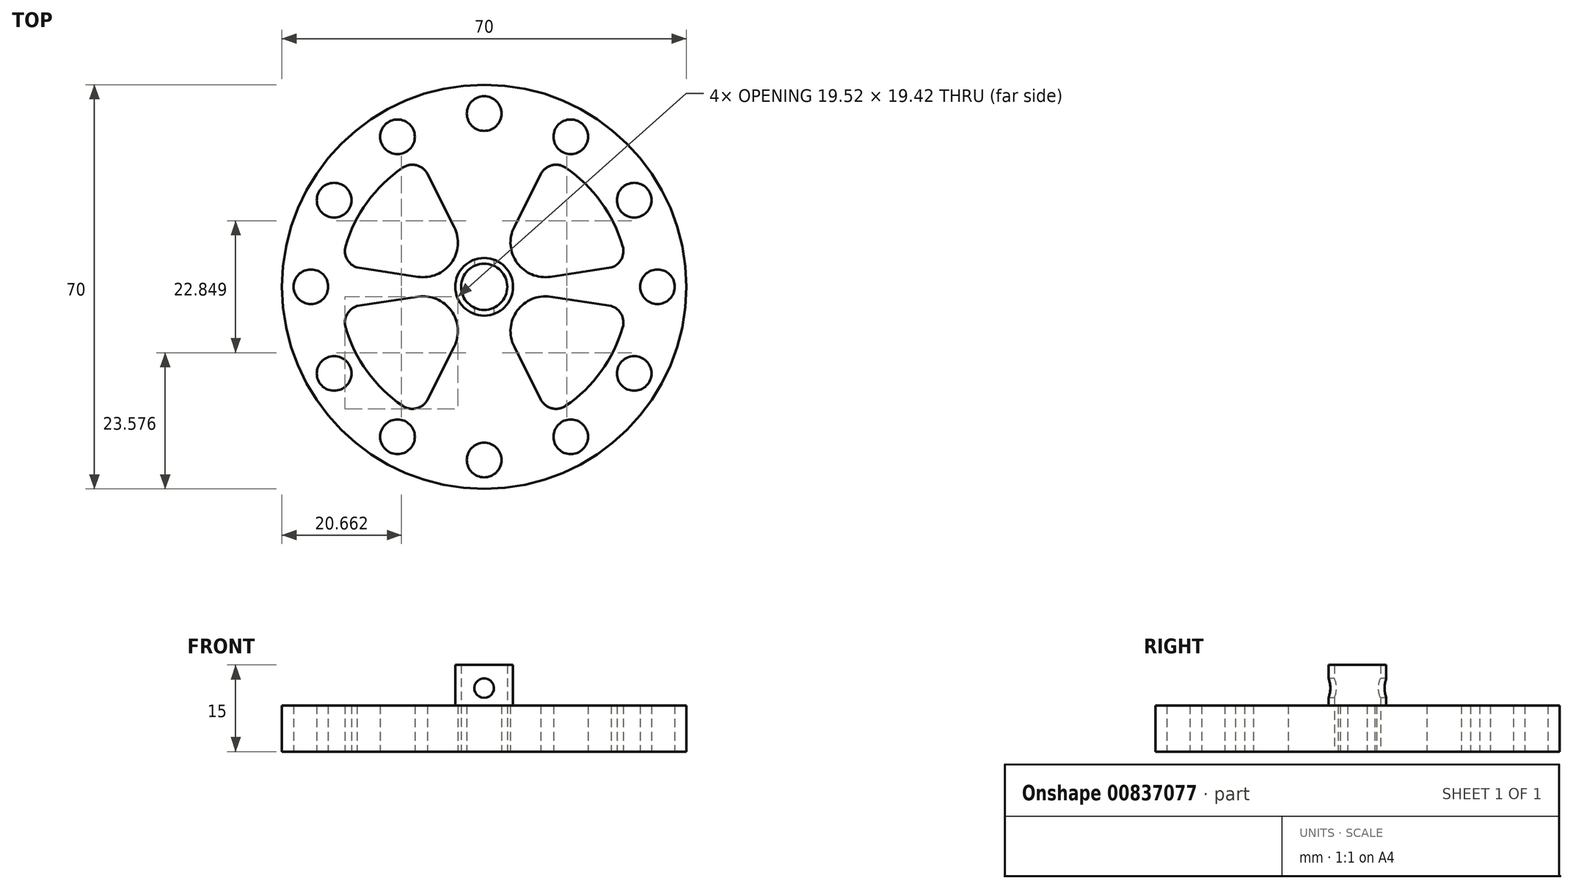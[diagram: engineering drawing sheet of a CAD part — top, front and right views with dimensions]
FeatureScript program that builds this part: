
annotation { "Feature Type Name" : "Feature", "Feature Type Description" : "" }
export const myFeature = defineFeature(function(context is Context, id is Id, definition is map)
    precondition{}
    {
        {
            var Q0;
            Q0=qCreatedBy(makeId("Top.planeOp"),FACE);
            var sketch = newSketch(context, id + "F0", { "sketchPlane" : qUnion([Q0])});
            skCircle(sketch, "E0", {"center": v(0, 0) * mm, "radius": 35 * mm});
            skCircle(sketch, "E1", {"center": v(0, 0) * mm, "radius": 30 * mm, "construction": true});
            skLineSegment(sketch, "E2", {"start": v(0, -35) * mm, "end": v(0, 59.95) * mm, "construction": true});
            skCircle(sketch, "E3", {"center": v(0, 30) * mm, "radius": 3 * mm});
            skCircle(sketch, "E4.1.0", {"center": v(-15, 25.98) * mm, "radius": 3 * mm});
            skCircle(sketch, "E4.2.0", {"center": v(-25.98, 15) * mm, "radius": 3 * mm});
            skCircle(sketch, "E5.1.3.0", {"center": v(-30, 0) * mm, "radius": 3 * mm});
            skCircle(sketch, "E5.1.4.0", {"center": v(-25.98, -15) * mm, "radius": 3 * mm});
            skCircle(sketch, "E5.1.5.0", {"center": v(-15, -25.98) * mm, "radius": 3 * mm});
            skCircle(sketch, "E5.1.6.0", {"center": v(0, -30) * mm, "radius": 3 * mm});
            skCircle(sketch, "E5.1.7.0", {"center": v(15, -25.98) * mm, "radius": 3 * mm});
            skCircle(sketch, "E5.1.8.0", {"center": v(25.98, -15) * mm, "radius": 3 * mm});
            skCircle(sketch, "E5.1.9.0", {"center": v(30, 0) * mm, "radius": 3 * mm});
            skCircle(sketch, "E5.1.10.0", {"center": v(25.98, 15) * mm, "radius": 3 * mm});
            skCircle(sketch, "E6.1.11.0", {"center": v(15, 25.98) * mm, "radius": 3 * mm});
            skCircle(sketch, "E7", {"center": v(0, 0) * mm, "radius": 4 * mm});
            skLineSegment(sketch, "E8", {"start": v(0, 0) * mm, "end": v(-61.25, 0) * mm, "construction": true});
            skArc(sketch, "E9.trimOffspring", {"start": v(-14.15, 20.6) * mm, "mid": v(-20.24, 14.68) * mm, "end": v(-23.99, 7.05) * mm});
            skPoint(sketch, "E10.visualSharp", {"position": v(-11.27, 22.31) * mm});
            skArc(sketch, "E10.filletArc", {"start": v(-9.8, 19.54) * mm, "mid": v(-11.74, 21.05) * mm, "end": v(-14.15, 20.6) * mm});
            skPoint(sketch, "E11.visualSharp", {"position": v(-24.06, 6.8) * mm});
            skArc(sketch, "E11.filletArc", {"start": v(-23.99, 7.05) * mm, "mid": v(-23.75, 4.78) * mm, "end": v(-21.99, 3.33) * mm});
            skLineSegment(sketch, "E12.MirrorCS", {"start": v(0, 0) * mm, "end": v(61.25, 0) * mm, "construction": true});
            skArc(sketch, "E13.MirrorCS", {"start": v(14.15, 20.6) * mm, "mid": v(20.24, 14.68) * mm, "end": v(23.99, 7.05) * mm});
            skArc(sketch, "E14.MirrorCS", {"start": v(9.8, 19.54) * mm, "mid": v(11.74, 21.05) * mm, "end": v(14.15, 20.6) * mm});
            skArc(sketch, "E15.MirrorCS", {"start": v(23.99, 7.05) * mm, "mid": v(23.75, 4.78) * mm, "end": v(21.99, 3.33) * mm});
            skArc(sketch, "E16.MirrorCS", {"start": v(-23.99, -7.05) * mm, "mid": v(-23.75, -4.78) * mm, "end": v(-21.99, -3.33) * mm});
            skArc(sketch, "E17.MirrorCS", {"start": v(-14.15, -20.6) * mm, "mid": v(-20.24, -14.68) * mm, "end": v(-23.99, -7.05) * mm});
            skArc(sketch, "E18.MirrorCS", {"start": v(-9.8, -19.54) * mm, "mid": v(-11.74, -21.05) * mm, "end": v(-14.15, -20.6) * mm});
            skArc(sketch, "E19.MirrorCS", {"start": v(23.99, -7.05) * mm, "mid": v(23.75, -4.78) * mm, "end": v(21.99, -3.33) * mm});
            skArc(sketch, "E20.MirrorCS", {"start": v(14.15, -20.6) * mm, "mid": v(20.24, -14.68) * mm, "end": v(23.99, -7.05) * mm});
            skArc(sketch, "E21.MirrorCS", {"start": v(9.8, -19.54) * mm, "mid": v(11.74, -21.05) * mm, "end": v(14.15, -20.6) * mm});
            skLineSegment(sketch, "E22", {"start": v(-5.2, 10.36) * mm, "end": v(-9.8, 19.54) * mm});
            skLineSegment(sketch, "E23", {"start": v(-11.46, 1.74) * mm, "end": v(-21.99, 3.33) * mm});
            skArc(sketch, "E24.filletArc", {"start": v(-11.46, 1.74) * mm, "mid": v(-5.7, 4.14) * mm, "end": v(-5.2, 10.36) * mm});
            skLineSegment(sketch, "E25", {"start": v(5.2, 10.36) * mm, "end": v(9.8, 19.54) * mm});
            skLineSegment(sketch, "E26", {"start": v(11.46, 1.74) * mm, "end": v(21.99, 3.33) * mm});
            skArc(sketch, "E27.filletArc", {"start": v(5.2, 10.36) * mm, "mid": v(5.7, 4.14) * mm, "end": v(11.46, 1.74) * mm});
            skLineSegment(sketch, "E28", {"start": v(11.46, -1.74) * mm, "end": v(21.99, -3.33) * mm});
            skLineSegment(sketch, "E29", {"start": v(5.2, -10.36) * mm, "end": v(9.8, -19.54) * mm});
            skLineSegment(sketch, "E30", {"start": v(-5.2, -10.36) * mm, "end": v(-9.8, -19.54) * mm});
            skLineSegment(sketch, "E31", {"start": v(-11.46, -1.74) * mm, "end": v(-21.99, -3.33) * mm});
            skArc(sketch, "E32.filletArc", {"start": v(-5.2, -10.36) * mm, "mid": v(-5.7, -4.14) * mm, "end": v(-11.46, -1.74) * mm});
            skArc(sketch, "E33.filletArc", {"start": v(11.46, -1.74) * mm, "mid": v(5.7, -4.14) * mm, "end": v(5.2, -10.36) * mm});
            skSolve(sketch);
        }
        {
            var Q0;
            Q0=makeQuery(id+"F0.imprint","IMPRINT",FACE,{"disambiguationData":[TD([[makeQuery(id+"F0.imprint","IMPRINT",EDGE,{"derivedFrom":sQuery(id+"F0.wireOp",EDGE,"E0")}),1.0]])]});
            extrude(context, id + "F1", {"entities" : qUnion([Q0]), "depth" : 8 * mm, "offsetDistance" : 25 * mm});
        }
        {
            var Q0;
            Q0=makeQuery(id+"F1.opExtrude","CAP_FACE",FACE,{"disambiguationData":[OSD([sQuery(id+"F0.wireOp",EDGE,"E0"),sQuery(id+"F0.wireOp",EDGE,"E3"),sQuery(id+"F0.wireOp",EDGE,"E4.1.0"),sQuery(id+"F0.wireOp",EDGE,"E4.2.0"),sQuery(id+"F0.wireOp",EDGE,"E5.1.3.0"),sQuery(id+"F0.wireOp",EDGE,"E5.1.4.0"),sQuery(id+"F0.wireOp",EDGE,"E5.1.5.0"),sQuery(id+"F0.wireOp",EDGE,"E5.1.6.0"),sQuery(id+"F0.wireOp",EDGE,"E5.1.7.0"),sQuery(id+"F0.wireOp",EDGE,"E5.1.8.0"),sQuery(id+"F0.wireOp",EDGE,"E5.1.9.0"),sQuery(id+"F0.wireOp",EDGE,"E5.1.10.0"),sQuery(id+"F0.wireOp",EDGE,"E6.1.11.0"),sQuery(id+"F0.wireOp",EDGE,"E7"),sQuery(id+"F0.wireOp",EDGE,"b72146d2-3762-48a1-aead-35699e50c76d.trimOffspring"),sQuery(id+"F0.wireOp",EDGE,"afd8dc76-549a-4bde-826f-224530018dbb.trimOffspring"),sQuery(id+"F0.wireOp",EDGE,"e26d6468-0bac-499e-aba4-d3ecb99095ac.trimOffspring"),sQuery(id+"F0.wireOp",EDGE,"E9.trimOffspring"),sQuery(id+"F0.wireOp",EDGE,"E10.filletArc"),sQuery(id+"F0.wireOp",EDGE,"E11.filletArc"),sQuery(id+"F0.wireOp",EDGE,"737ca254-2220-4df8-a228-9b079c625d56.filletArc"),sQuery(id+"F0.wireOp",EDGE,"4ca716ca-37b9-4d79-854d-2ad836eb5197.filletArc"),sQuery(id+"F0.wireOp",EDGE,"9ba0dc1a-9e89-474d-9ec4-13eb95947f0b0.MirrorCS"),sQuery(id+"F0.wireOp",EDGE,"E13.MirrorCS"),sQuery(id+"F0.wireOp",EDGE,"E14.MirrorCS"),sQuery(id+"F0.wireOp",EDGE,"14f18adf-acc9-4e33-beb3-9d87d2d503e00.MirrorCS"),sQuery(id+"F0.wireOp",EDGE,"E15.MirrorCS"),sQuery(id+"F0.wireOp",EDGE,"bb298522-1bb2-4c82-8dc1-17a1577af3e00.MirrorCS"),sQuery(id+"F0.wireOp",EDGE,"1103edbf-a456-4de8-b66d-61f0f39e1d8d0.MirrorCS"),sQuery(id+"F0.wireOp",EDGE,"bfebdde4-4062-42d0-814a-6997603a60e70.MirrorCS"),sQuery(id+"F0.wireOp",EDGE,"6658f62d-90ea-487c-a8c0-3a889d28ed9b0.MirrorCS"),sQuery(id+"F0.wireOp",EDGE,"E16.MirrorCS"),sQuery(id+"F0.wireOp",EDGE,"E17.MirrorCS"),sQuery(id+"F0.wireOp",EDGE,"E18.MirrorCS"),sQuery(id+"F0.wireOp",EDGE,"6907d86f-5a30-4c55-b35b-3e21709d221b0.MirrorCS"),sQuery(id+"F0.wireOp",EDGE,"a9cb69c4-9af4-4031-b75a-734ece7c0d570.MirrorCS"),sQuery(id+"F0.wireOp",EDGE,"32e31fb0-95ab-41e4-a7ee-95fffdf824af0.MirrorCS"),sQuery(id+"F0.wireOp",EDGE,"999fac1f-35e1-4174-ba6a-6df3bfaa67fa0.MirrorCS"),sQuery(id+"F0.wireOp",EDGE,"096059d6-0ce7-4c35-9d6f-320af6c8830b0.MirrorCS"),sQuery(id+"F0.wireOp",EDGE,"E19.MirrorCS"),sQuery(id+"F0.wireOp",EDGE,"E20.MirrorCS"),sQuery(id+"F0.wireOp",EDGE,"E21.MirrorCS"),sQuery(id+"F0.wireOp",EDGE,"88a787ff-a97b-4f67-adac-4956d4b8e64f0.MirrorCS"),sQuery(id+"F0.wireOp",EDGE,"b39a0d89-169a-4836-b0d1-d3890d00fc380.MirrorCS"),sQuery(id+"F0.wireOp",EDGE,"bff1478b-b53a-408e-bb93-e75efda595f40.MirrorCS"),sQuery(id+"F0.wireOp",EDGE,"cd460a81-fdbf-43d0-bb42-aa287db955ff0.MirrorCS")])],"isStart":false});
            var sketch = newSketch(context, id + "F2", { "sketchPlane" : qUnion([Q0])});
            skCircle(sketch, "E34", {"center": v(0, 0) * mm, "radius": 5 * mm});
            skSolve(sketch);
        }
        {
            var Q0;
            Q0=makeQuery(id+"F2.imprint","IMPRINT",FACE,{"disambiguationData":[TD([[makeQuery(id+"F2.imprint","IMPRINT",EDGE,{"derivedFrom":sQuery(id+"F2.wireOp",EDGE,"E34")}),1.0]])]});
            extrude(context, id + "F3", {"entities" : qUnion([Q0]), "operationType" : NewBodyOperationType.ADD, "depth" : 7 * mm, "offsetDistance" : 25 * mm});
        }
        {
            var Q0;
            Q0=qCreatedBy(makeId("Front.planeOp"),FACE);
            cPlane(context, id + "F4", {"entities" : qUnion([Q0]), "cplaneType" : CPlaneType.OFFSET, "offset" : 5 * mm, "width" : 150 * mm, "height" : 150 * mm});
        }
        {
            var Q0;
            Q0=qCreatedBy(id+"F4.planeOp",FACE);
            var sketch = newSketch(context, id + "F5", { "sketchPlane" : qUnion([Q0])});
            skLineSegment(sketch, "E35", {"start": v(0, 0) * mm, "end": v(0, 24.47) * mm, "construction": true});
            skLineSegment(sketch, "E36", {"start": v(-10.6, 11) * mm, "end": v(0, 11) * mm, "construction": true});
            skLineSegment(sketch, "E37", {"start": v(0, 0) * mm, "end": v(-21.75, 0) * mm, "construction": true});
            skPoint(sketch, "E38", {"position": v(0, 11) * mm});
            skSolve(sketch);
        }
        {
            var Q0;
            Q0=sQuery(id+"F5.wireOp",VERTEX,"E38");
            var Q1;
            Q1=makeQuery(id+"F1.opExtrude","SWEPT_BODY",BODY,{"disambiguationData":[OSD([sQuery(id+"F0.wireOp",EDGE,"E0"),sQuery(id+"F0.wireOp",EDGE,"E3"),sQuery(id+"F0.wireOp",EDGE,"E4.1.0"),sQuery(id+"F0.wireOp",EDGE,"E4.2.0"),sQuery(id+"F0.wireOp",EDGE,"E5.1.3.0"),sQuery(id+"F0.wireOp",EDGE,"E5.1.4.0"),sQuery(id+"F0.wireOp",EDGE,"E5.1.5.0"),sQuery(id+"F0.wireOp",EDGE,"E5.1.6.0"),sQuery(id+"F0.wireOp",EDGE,"E5.1.7.0"),sQuery(id+"F0.wireOp",EDGE,"E5.1.8.0"),sQuery(id+"F0.wireOp",EDGE,"E5.1.9.0"),sQuery(id+"F0.wireOp",EDGE,"E5.1.10.0"),sQuery(id+"F0.wireOp",EDGE,"E6.1.11.0"),sQuery(id+"F0.wireOp",EDGE,"E7"),sQuery(id+"F0.wireOp",EDGE,"b72146d2-3762-48a1-aead-35699e50c76d.trimOffspring"),sQuery(id+"F0.wireOp",EDGE,"afd8dc76-549a-4bde-826f-224530018dbb.trimOffspring"),sQuery(id+"F0.wireOp",EDGE,"e26d6468-0bac-499e-aba4-d3ecb99095ac.trimOffspring"),sQuery(id+"F0.wireOp",EDGE,"E9.trimOffspring"),sQuery(id+"F0.wireOp",EDGE,"E10.filletArc"),sQuery(id+"F0.wireOp",EDGE,"E11.filletArc"),sQuery(id+"F0.wireOp",EDGE,"737ca254-2220-4df8-a228-9b079c625d56.filletArc"),sQuery(id+"F0.wireOp",EDGE,"4ca716ca-37b9-4d79-854d-2ad836eb5197.filletArc"),sQuery(id+"F0.wireOp",EDGE,"9ba0dc1a-9e89-474d-9ec4-13eb95947f0b0.MirrorCS"),sQuery(id+"F0.wireOp",EDGE,"E13.MirrorCS"),sQuery(id+"F0.wireOp",EDGE,"E14.MirrorCS"),sQuery(id+"F0.wireOp",EDGE,"14f18adf-acc9-4e33-beb3-9d87d2d503e00.MirrorCS"),sQuery(id+"F0.wireOp",EDGE,"E15.MirrorCS"),sQuery(id+"F0.wireOp",EDGE,"bb298522-1bb2-4c82-8dc1-17a1577af3e00.MirrorCS"),sQuery(id+"F0.wireOp",EDGE,"1103edbf-a456-4de8-b66d-61f0f39e1d8d0.MirrorCS"),sQuery(id+"F0.wireOp",EDGE,"bfebdde4-4062-42d0-814a-6997603a60e70.MirrorCS"),sQuery(id+"F0.wireOp",EDGE,"6658f62d-90ea-487c-a8c0-3a889d28ed9b0.MirrorCS"),sQuery(id+"F0.wireOp",EDGE,"E16.MirrorCS"),sQuery(id+"F0.wireOp",EDGE,"E17.MirrorCS"),sQuery(id+"F0.wireOp",EDGE,"E18.MirrorCS"),sQuery(id+"F0.wireOp",EDGE,"6907d86f-5a30-4c55-b35b-3e21709d221b0.MirrorCS"),sQuery(id+"F0.wireOp",EDGE,"a9cb69c4-9af4-4031-b75a-734ece7c0d570.MirrorCS"),sQuery(id+"F0.wireOp",EDGE,"32e31fb0-95ab-41e4-a7ee-95fffdf824af0.MirrorCS"),sQuery(id+"F0.wireOp",EDGE,"999fac1f-35e1-4174-ba6a-6df3bfaa67fa0.MirrorCS"),sQuery(id+"F0.wireOp",EDGE,"096059d6-0ce7-4c35-9d6f-320af6c8830b0.MirrorCS"),sQuery(id+"F0.wireOp",EDGE,"E19.MirrorCS"),sQuery(id+"F0.wireOp",EDGE,"E20.MirrorCS"),sQuery(id+"F0.wireOp",EDGE,"E21.MirrorCS"),sQuery(id+"F0.wireOp",EDGE,"88a787ff-a97b-4f67-adac-4956d4b8e64f0.MirrorCS"),sQuery(id+"F0.wireOp",EDGE,"b39a0d89-169a-4836-b0d1-d3890d00fc380.MirrorCS"),sQuery(id+"F0.wireOp",EDGE,"bff1478b-b53a-408e-bb93-e75efda595f40.MirrorCS"),sQuery(id+"F0.wireOp",EDGE,"cd460a81-fdbf-43d0-bb42-aa287db955ff0.MirrorCS")])]});
            hole(context, id + "F6", {"style" : HoleStyle.SIMPLE, "endStyle" : HoleEndStyle.THROUGH, "standardTappedOrClearance" : lookupTablePath({ "fit" : "Normal", "standard" : "ISO", "size" : "M3", "type" : "Clearance" }), "standardBlindInLast" : lookupTablePath({ "fit" : "Normal", "standard" : "ISO", "engagement" : "75%", "pitch" : "0.5 mm", "size" : "M3", "type" : "Clearance & tapped" }), "holeDiameter" : 3.4 * mm, "majorDiameter" : 5 * mm, "isTappedThrough" : true, "tappedDepth" : 12 * mm, "tapClearance" : 3, "startFromSketch" : true, "locations" : qUnion([Q0]), "scope" : qUnion([Q1])});
        }
    });
